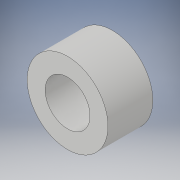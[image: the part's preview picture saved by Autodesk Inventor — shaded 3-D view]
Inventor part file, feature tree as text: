
AUTODESK INVENTOR PART (.ipt)
format: ipt  version: 2018 (Build 220112000, 112)  size: 98,304 bytes
history: native  units: in
note: dims shown in document units (in); Inventor stores cm internally (conversion verified against a paired STEP export)
features: extrude x1, sketch x1
ambient origin geometry x8: Origin, YZ Plane, XZ Plane, XY Plane, X Axis, Y Axis, Z Axis, Center Point
bodies: Solid1 (feature_tree)
feature tree (2):
  extrude  "Extrusion1"  Depth=0.1969in
  sketch  "Sketch1"  dims[d0=0.0787in d1=0.1969in d2=0.1969in d3=0.0in]
